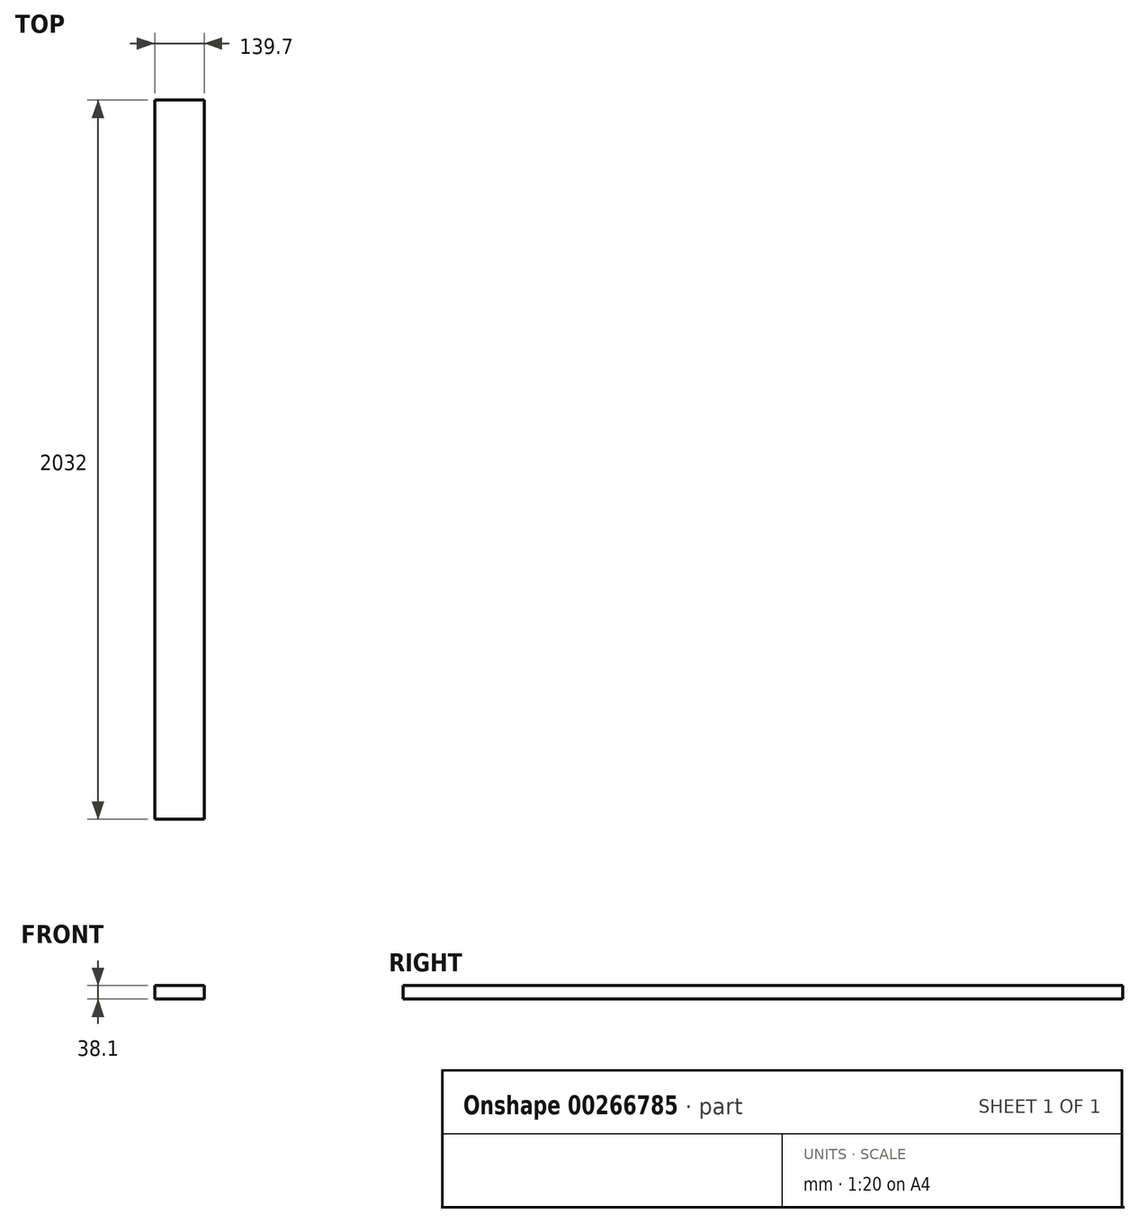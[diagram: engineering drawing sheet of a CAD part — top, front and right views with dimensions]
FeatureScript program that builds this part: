
annotation { "Feature Type Name" : "Feature", "Feature Type Description" : "" }
export const myFeature = defineFeature(function(context is Context, id is Id, definition is map)
    precondition{}
    {
        {
            var Q0;
            Q0=qCreatedBy(makeId("Front.planeOp"),FACE);
            var sketch = newSketch(context, id + "F0", { "sketchPlane" : qUnion([Q0])});
            skLineSegment(sketch, "E0.bottom", {"start": v(-48.34, 23.68) * mm, "end": v(91.36, 23.68) * mm});
            skLineSegment(sketch, "E0.top", {"start": v(-48.34, -14.42) * mm, "end": v(91.36, -14.42) * mm});
            skLineSegment(sketch, "E0.left", {"start": v(-48.34, 23.68) * mm, "end": v(-48.34, -14.42) * mm});
            skLineSegment(sketch, "E0.right", {"start": v(91.36, 23.68) * mm, "end": v(91.36, -14.42) * mm});
            skSolve(sketch);
        }
        {
            var Q0;
            Q0 = qSketchRegion(id + "F0", true);
            extrude(context, id + "F1", {"entities" : qUnion([Q0]), "depth" : 2032 * mm});
        }
    });
